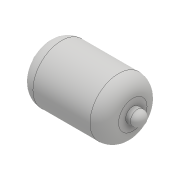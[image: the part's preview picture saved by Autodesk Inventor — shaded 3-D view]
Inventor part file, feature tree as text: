
AUTODESK INVENTOR PART (.ipt)
format: ipt  version: 2017 (Build 210142000, 142)  size: 134,144 bytes
history: native  units: mm
features: fillet x3, sketch x2, revolve x1, extrude x1, mirror x1
ambient origin geometry x8: Origin, YZ Plane, XZ Plane, XY Plane, X Axis, Y Axis, Z Axis, Center Point
bodies: Solid1 (feature_tree)
feature tree (8):
  revolve  "Revolution1"  [1 undecoded]
  extrude  "Extrusion1"  Depth=3.0mm
  fillet  "Fillet1"  Radius=2.5mm
  mirror  "Mirror1"
  fillet  "Fillet2"  Radius=1.5mm
  fillet  "Fillet3"  Radius=1.5mm
  sketch  "Sketch1"  dims[d0=18.0mm d1=12.0mm]
  sketch  "Sketch2"  dims[d2=90.0deg d3=3.0mm d4=2.5mm d5=0.0mm d6=1.5mm d7=1.5mm d8=3.0mm]
note: 1 required parameter value undecoded (feature->parameter linkage not recoverable at this tier; creation-order binding heuristic only, values carry confidence <= 0.55)
